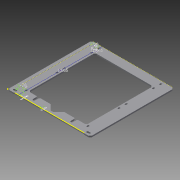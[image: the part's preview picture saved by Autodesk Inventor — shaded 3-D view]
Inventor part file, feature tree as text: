
AUTODESK INVENTOR PART (.ipt)
format: ipt  version: 2015 (Build 190159000, 159)  size: 243,200 bytes
history: native  units: mm
features: extrude x5, sketch x5
ambient origin geometry x8: Origin, YZ Plane, XZ Plane, XY Plane, X Axis, Y Axis, Z Axis, Center Point
bodies: Solid1 (feature_tree)
feature tree (10):
  extrude  "Extrusion1"  Depth=25.0mm
  extrude  "Extrusion2"  Depth=4.0mm
  extrude  "Extrusion3"  Depth=4.0mm
  extrude  "Extrusion4"  Depth=7.0mm
  extrude  "Extrusion5"  Depth=2.0mm
  sketch  "Sketch8"  dims[d40=10.0mm d41=0.0mm d42=2.0mm d43=135.0deg d44=20.0mm d45=20.0mm d46=10.0mm d47=0.0mm d48=9.0mm d49=8.75mm d50=6.5mm d51=32.3mm d52=9.257mm d53=32.3mm d54=164.35mm d55=34.65mm d56=10.0mm d57=0.0mm d58=8.0mm d59=8.0mm d60=8.511mm d61=16.026mm d62=10.0mm d63=0.0mm d64=4.0mm d65=4.0mm d66=11.65mm d67=3.25mm d68=20.0mm d69=20.0mm d70=11.65mm d72=20.0mm]
  sketch  "Sketch1"  dims[d17=0.0mm d30=25.0mm]
  sketch  "Sketch4"  dims[d31=4.0mm d32=4.0mm]
  sketch  "Sketch5"  dims[d33=4.0mm d34=4.0mm]
  sketch  "Sketch7"  dims[d36=7.0mm d37=7.0mm]
